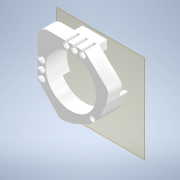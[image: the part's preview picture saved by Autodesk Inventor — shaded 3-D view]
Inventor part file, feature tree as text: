
AUTODESK INVENTOR PART (.ipt)
format: ipt  version: 2022 (Build 260153000, 153)  size: 1,150,976 bytes
history: native  units: in
note: dims shown in document units (in); Inventor stores cm internally (conversion verified against a paired STEP export)
features: reference x7, extrude x5, fillet x4, sketch x4, chamfer x4, other x4, projected_geometry x3, plane x2, pattern_circular x1
ambient origin geometry x8: Origin, YZ Plane, XZ Plane, XY Plane, X Axis, Y Axis, Z Axis, Center Point
bodies: Solid1 (feature_tree)
feature tree (34):
  plane  "Work Plane1"
  extrude  "Extrusion1"  Depth=0.0394in TaperAngle=0.0deg
  fillet  "Fillet1"  Radius=0.0394in
  sketch  "Sketch2"  dims[d10=0.4724in d11=0.0in d12=0.15in d13=0.0in]
  plane  "Work Plane2"
  extrude  "Extrusion2"  Depth=0.15in TaperAngle=0.0deg
  extrude  "Extrusion3"  Depth=1.5in
  chamfer  "Chamfer4"  Distance=2.0in
  fillet  "Fillet4"  Radius=3.1in
  fillet  "Fillet5"  Radius=1.1811in
  pattern_circular  "Circular Pattern1"  Angle=45.0deg  [1 undecoded]
  chamfer  "Chamfer2"  Distance=0.0236in Angle=45.0deg
  chamfer  "Chamfer3"  Distance=0.1106in Angle=45.0deg
  extrude  "Extrusion5"  Depth=0.0394in
  chamfer  "Chamfer5"  Distance=0.1969in
  fillet  "Fillet6"  Radius=0.0472in
  extrude  "Extrusion6"  Depth=0.2756in
  sketch  "Sketch1"  dims[d0=1.2598in d1=0.4724in d2=0.0in d3=0.0394in]
  reference  "Reference1"
  reference  "Reference2"
  reference  "Reference8"
  reference  "Reference9"
  reference  "Reference10"
  sketch  "Sketch3"  dims[d17=1.1811in d18=360.0deg d20=1.5in]
  reference  "Reference11"
  projected_geometry  "Projected Loop7"
  projected_geometry  "Projected Loop8"
  projected_geometry  "Projected Loop9"
  reference  "Reference12"
  sketch  "Sketch6"  dims[d21=1.5in d22=2.0in d23=3.1in d24=1.1811in d26=360.0deg d28=0.0236in d29=0.125in d30=45.0deg d31=0.0236in d32=0.125in d33=45.0deg d34=0.1106in d35=0.125in d36=45.0deg d48=0.0394in d49=0.1969in d50=0.0472in d51=0.2756in d52=0.7723in d53=0.0in d54=0.0472in d55=0.125in d56=45.0deg d59=45.0deg d60=0.0472in d61=1.0in d62=0.0in]
  other  "<userpath>\Documents\CAD\guardSwerve1\Assembly1.iam"
  other  "Assembly1.iam"
  other  "lower_plate:1"
  other  "uppermidblock:1"
note: 1 required parameter value undecoded (feature->parameter linkage not recoverable at this tier; creation-order binding heuristic only, values carry confidence <= 0.55)
